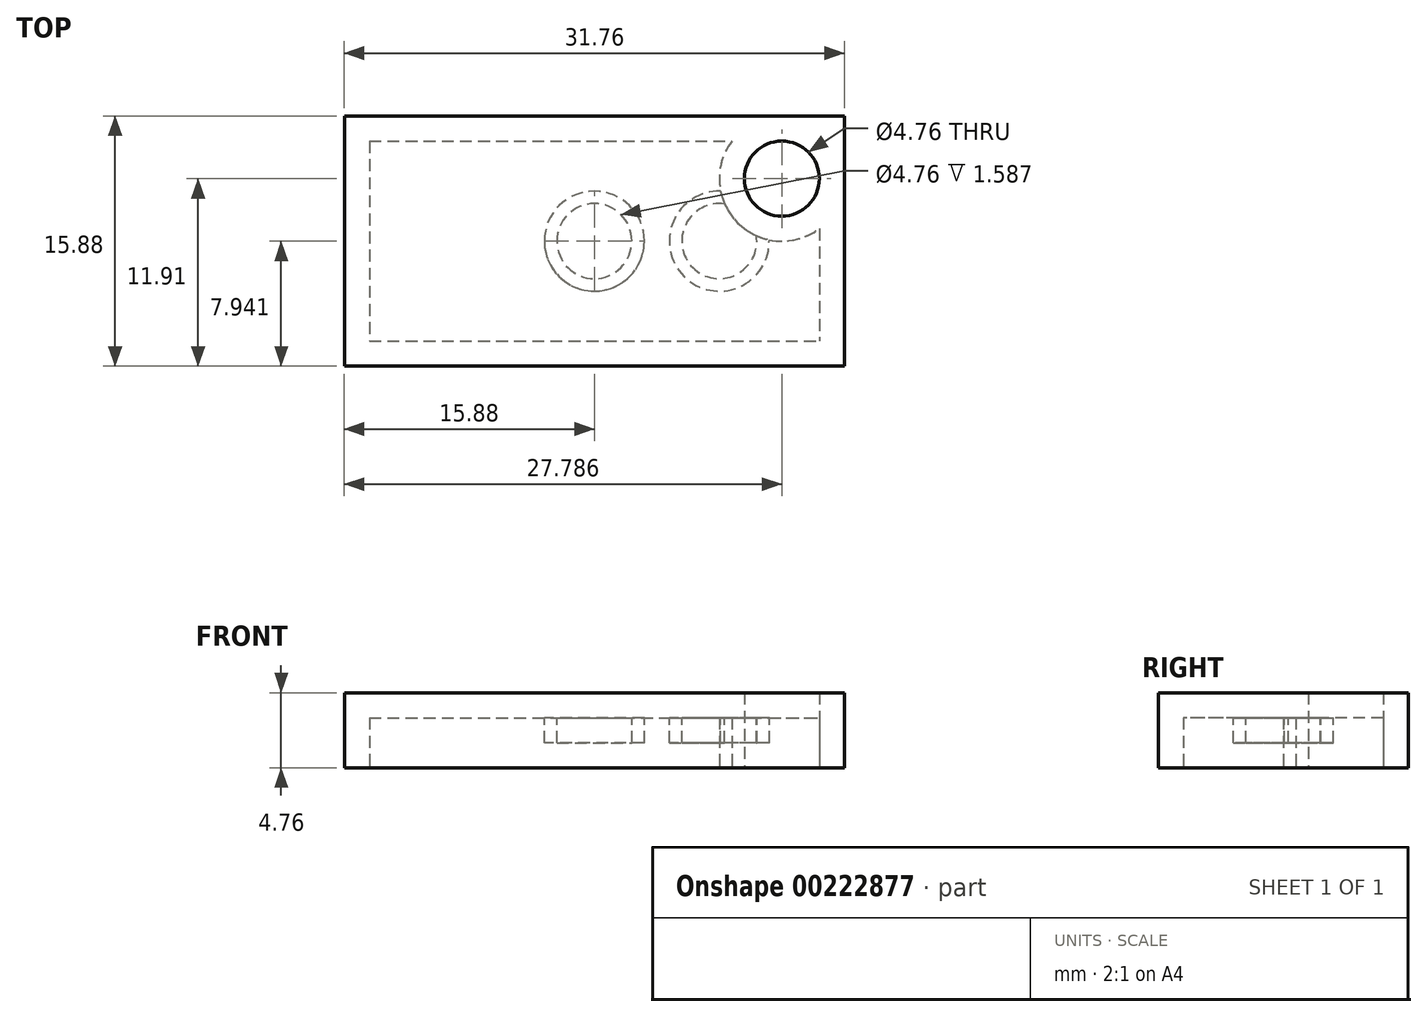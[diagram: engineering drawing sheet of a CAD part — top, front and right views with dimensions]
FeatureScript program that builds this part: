
annotation { "Feature Type Name" : "Feature", "Feature Type Description" : "" }
export const myFeature = defineFeature(function(context is Context, id is Id, definition is map)
    precondition{}
    {
        {
            var Q0;
            Q0=qCreatedBy(makeId("Top.planeOp"),FACE);
            var sketch = newSketch(context, id + "F0", { "sketchPlane" : qUnion([Q0])});
            skLineSegment(sketch, "E0.bottom", {"start": v(-15.88, 3.97) * mm, "end": v(15.87, 3.97) * mm});
            skLineSegment(sketch, "E0.top", {"start": v(-15.88, -11.9) * mm, "end": v(15.87, -11.9) * mm});
            skLineSegment(sketch, "E0.left", {"start": v(-15.88, 3.97) * mm, "end": v(-15.88, -11.9) * mm});
            skLineSegment(sketch, "E0.right", {"start": v(15.88, 3.97) * mm, "end": v(15.88, -11.9) * mm});
            skPoint(sketch, "E0.middle", {"position": v(0, 0) * mm});
            skCircle(sketch, "E1", {"center": v(-11.9, 0) * mm, "radius": 2.38 * mm});
            skCircle(sketch, "E2.MirrorC", {"center": v(11.9, 0) * mm, "radius": 2.38 * mm});
            skCircle(sketch, "E3.1.0.0", {"center": v(-3.97, 0) * mm, "radius": 2.38 * mm});
            skCircle(sketch, "E3.2.0.0", {"center": v(3.97, 0) * mm, "radius": 2.38 * mm});
            skLineSegment(sketch, "E3.direction1", {"start": v(-11.9, 0) * mm, "end": v(-3.97, 0) * mm, "construction": true});
            skCircle(sketch, "E4", {"center": v(-11.9, -7.94) * mm, "radius": 2.35 * mm});
            skLineSegment(sketch, "E5", {"start": v(-11.9, 0) * mm, "end": v(-11.9, -7.94) * mm});
            skCircle(sketch, "E6.1.0.0", {"center": v(-3.97, -7.94) * mm, "radius": 2.35 * mm});
            skCircle(sketch, "E6.2.0.0", {"center": v(3.97, -7.94) * mm, "radius": 2.35 * mm});
            skCircle(sketch, "E6.3.0.0", {"center": v(11.9, -7.94) * mm, "radius": 2.35 * mm});
            skLineSegment(sketch, "E6.direction1", {"start": v(-11.9, -7.94) * mm, "end": v(-3.97, -7.94) * mm, "construction": true});
            skSolve(sketch);
        }
        {
            var Q0;
            Q0=makeQuery(id+"F0.imprint","IMPRINT",FACE,{"disambiguationData":[TD([[makeQuery(id+"F0.imprint","IMPRINT",EDGE,{"derivedFrom":sQuery(id+"F0.wireOp",EDGE,"E0.bottom")}),-1.0]])]});
            extrude(context, id + "F1", {"entities" : qUnion([Q0]), "depth" : 3.17 * mm});
        }
        {
            var Q0;
            Q0=makeQuery(id+"F0.imprint","IMPRINT",FACE,{"disambiguationData":[TD([[makeQuery(id+"F0.imprint","IMPRINT",EDGE,{"derivedFrom":sQuery(id+"F0.wireOp",EDGE,"E2.MirrorC")}),-1.0]])]});
            var Q1;
            Q1=makeQuery(id+"F0.imprint","IMPRINT",FACE,{"disambiguationData":[TD([[makeQuery(id+"F0.imprint","IMPRINT",EDGE,{"derivedFrom":sQuery(id+"F0.wireOp",EDGE,"E1")}),1.0]])]});
            var Q2;
            Q2=makeQuery(id+"F0.imprint","IMPRINT",FACE,{"disambiguationData":[TD([[makeQuery(id+"F0.imprint","IMPRINT",EDGE,{"derivedFrom":sQuery(id+"F0.wireOp",EDGE,"E3.2.0.0")}),1.0]])]});
            var Q3;
            Q3=makeQuery(id+"F0.imprint","IMPRINT",FACE,{"disambiguationData":[TD([[makeQuery(id+"F0.imprint","IMPRINT",EDGE,{"derivedFrom":sQuery(id+"F0.wireOp",EDGE,"E3.1.0.0")}),1.0]])]});
            var Q4;
            Q4=makeQuery(id+"F0.imprint","IMPRINT",FACE,{"disambiguationData":[TD([[makeQuery(id+"F0.imprint","IMPRINT",EDGE,{"derivedFrom":sQuery(id+"F0.wireOp",EDGE,"E4")}),1.0]])]});
            var Q5;
            Q5=makeQuery(id+"F0.imprint","IMPRINT",FACE,{"disambiguationData":[TD([[makeQuery(id+"F0.imprint","IMPRINT",EDGE,{"derivedFrom":sQuery(id+"F0.wireOp",EDGE,"E6.1.0.0")}),1.0]])]});
            var Q6;
            Q6=makeQuery(id+"F0.imprint","IMPRINT",FACE,{"disambiguationData":[TD([[makeQuery(id+"F0.imprint","IMPRINT",EDGE,{"derivedFrom":sQuery(id+"F0.wireOp",EDGE,"E6.2.0.0")}),1.0]])]});
            var Q7;
            Q7=makeQuery(id+"F0.imprint","IMPRINT",FACE,{"disambiguationData":[TD([[makeQuery(id+"F0.imprint","IMPRINT",EDGE,{"derivedFrom":sQuery(id+"F0.wireOp",EDGE,"E6.3.0.0")}),1.0]])]});
            extrude(context, id + "F2", {"entities" : qUnion([Q0, Q1, Q2, Q3, Q4, Q5, Q6, Q7]), "operationType" : NewBodyOperationType.ADD, "depth" : 4.76 * mm});
        }
        {
            var Q0;
            {var subQ0=sQuery(id+"F0.wireOp",EDGE,"E2.MirrorC");var subQ1=sQuery(id+"F0.wireOp",EDGE,"E1");Q0=makeQuery(id+"F2.boolean.opBoolean","MERGE",FACE,{"derivedFrom":[makeQuery(id+"F1.opExtrude","CAP_FACE",FACE,{"disambiguationData":[OSD([sQuery(id+"F0.wireOp",EDGE,"E0.bottom"),sQuery(id+"F0.wireOp",EDGE,"E0.top"),sQuery(id+"F0.wireOp",EDGE,"E0.left"),sQuery(id+"F0.wireOp",EDGE,"E0.right"),subQ1,subQ0])],"isStart":true}),makeQuery(id+"F2.opExtrude","CAP_FACE",FACE,{"disambiguationData":[OSD([subQ1])],"isStart":true}),makeQuery(id+"F2.opExtrude","CAP_FACE",FACE,{"disambiguationData":[OSD([subQ0])],"isStart":true})]});}
            shell(context, id + "F3", {"entities" : qUnion([Q0]), "thickness" : 1.59 * mm});
        }
        {
            var Q0;
            Q0=makeQuery(id+"F3.opShell","OFFSET_FACE",FACE,{"disambiguationData":[OSD([sQuery(id+"F0.wireOp",EDGE,"E0.bottom"),sQuery(id+"F0.wireOp",EDGE,"E0.top"),sQuery(id+"F0.wireOp",EDGE,"E0.left"),sQuery(id+"F0.wireOp",EDGE,"E0.right"),sQuery(id+"F0.wireOp",EDGE,"E1"),sQuery(id+"F0.wireOp",EDGE,"E2.MirrorC")])]});
            var sketch = newSketch(context, id + "F4", { "sketchPlane" : qUnion([Q0])});
            skLineSegment(sketch, "E7", {"start": v(-11.9, 7.94) * mm, "end": v(-3.97, 0) * mm});
            skCircle(sketch, "E8", {"center": v(-7.94, 3.97) * mm, "radius": 3.18 * mm});
            skCircle(sketch, "E9.0", {"center": v(-7.94, 3.97) * mm, "radius": 2.38 * mm});
            skCircle(sketch, "E10.1.0.0", {"center": v(0, 3.97) * mm, "radius": 3.18 * mm});
            skCircle(sketch, "E10.1.0.1", {"center": v(0, 3.97) * mm, "radius": 2.38 * mm});
            skCircle(sketch, "E10.2.0.0", {"center": v(7.94, 3.97) * mm, "radius": 3.18 * mm});
            skCircle(sketch, "E10.2.0.1", {"center": v(7.94, 3.97) * mm, "radius": 2.38 * mm});
            skLineSegment(sketch, "E10.direction1", {"start": v(-7.94, 3.97) * mm, "end": v(0, 3.97) * mm, "construction": true});
            skSolve(sketch);
        }
        {
            var Q0;
            {var subQ0=sQuery(id+"F4.wireOp",EDGE,"E8");var subQ1=sQuery(id+"F4.wireOp",EDGE,"E7");var subQ2=makeQuery(id+"F4.imprint","INTERSECT",VERTEX,{"disambiguationData":[OD(0.0)],"derivedFrom":[subQ1,subQ0]});Q0=makeQuery(id+"F4.imprint","IMPRINT",FACE,{"disambiguationData":[TD([[makeQuery(id+"F4.imprint","IMPRINT",EDGE,{"disambiguationData":[TD([[subQ2,-1.0]])],"derivedFrom":subQ1}),-1.0]])]});}
            var Q1;
            {var subQ0=sQuery(id+"F4.wireOp",EDGE,"E8");var subQ1=sQuery(id+"F4.wireOp",EDGE,"E7");var subQ2=makeQuery(id+"F4.imprint","INTERSECT",VERTEX,{"disambiguationData":[OD(0.0)],"derivedFrom":[subQ1,subQ0]});Q1=makeQuery(id+"F4.imprint","IMPRINT",FACE,{"disambiguationData":[TD([[makeQuery(id+"F4.imprint","IMPRINT",EDGE,{"disambiguationData":[TD([[subQ2,-1.0]])],"derivedFrom":subQ1}),1.0]])]});}
            var Q2;
            Q2=makeQuery(id+"F4.imprint","IMPRINT",FACE,{"disambiguationData":[TD([[makeQuery(id+"F4.imprint","IMPRINT",EDGE,{"derivedFrom":sQuery(id+"F4.wireOp",EDGE,"E10.1.0.0")}),1.0]])]});
            var Q3;
            Q3=makeQuery(id+"F4.imprint","IMPRINT",FACE,{"disambiguationData":[TD([[makeQuery(id+"F4.imprint","IMPRINT",EDGE,{"derivedFrom":sQuery(id+"F4.wireOp",EDGE,"E10.2.0.0")}),1.0]])]});
            extrude(context, id + "F5", {"entities" : qUnion([Q0, Q1, Q2, Q3]), "operationType" : NewBodyOperationType.ADD, "depth" : 1.59 * mm});
        }
    });
